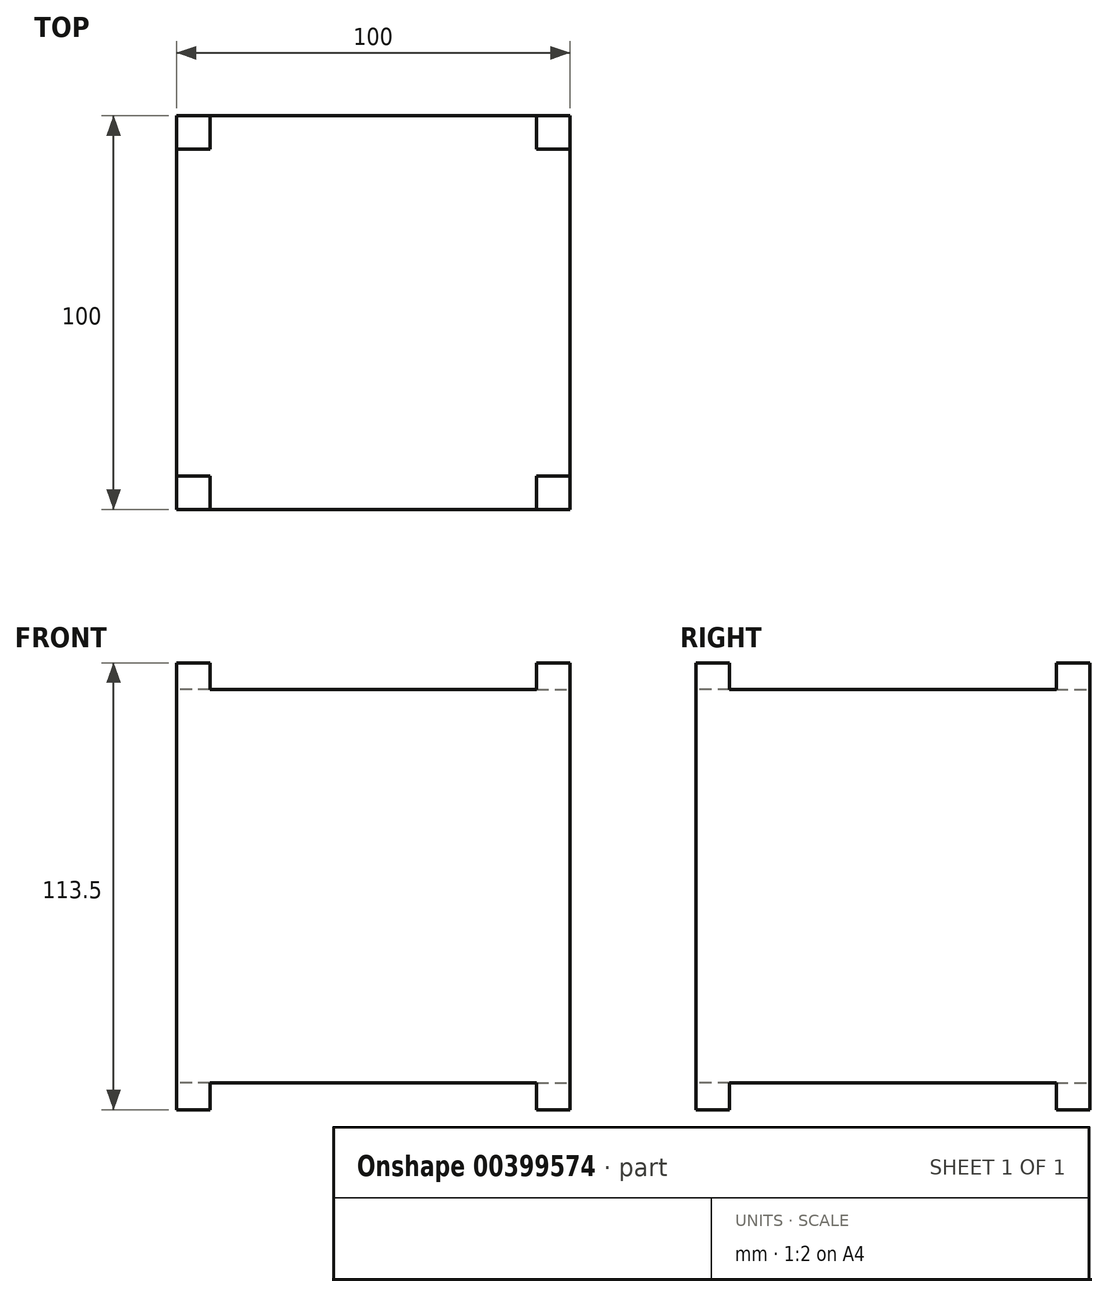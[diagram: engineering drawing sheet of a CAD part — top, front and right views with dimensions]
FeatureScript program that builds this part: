
annotation { "Feature Type Name" : "Feature", "Feature Type Description" : "" }
export const myFeature = defineFeature(function(context is Context, id is Id, definition is map)
    precondition{}
    {
        {
            var Q0;
            Q0=qCreatedBy(makeId("Top.planeOp"),FACE);
            var sketch = newSketch(context, id + "F0", { "sketchPlane" : qUnion([Q0])});
            skLineSegment(sketch, "E0.bottom", {"start": v(-50, 50) * mm, "end": v(50, 50) * mm});
            skLineSegment(sketch, "E0.top", {"start": v(-50, -50) * mm, "end": v(50, -50) * mm});
            skLineSegment(sketch, "E0.left", {"start": v(-50, 50) * mm, "end": v(-50, -50) * mm});
            skLineSegment(sketch, "E0.right", {"start": v(50, 50) * mm, "end": v(50, -50) * mm});
            skSolve(sketch);
        }
        {
            var Q0;
            Q0 = qSketchRegion(id + "F0", true);
            extrude(context, id + "F1", {"entities" : qUnion([Q0]), "endBound" : BoundingType.SYMMETRIC, "depth" : 100 * mm, "offsetDistance" : 25 * mm});
        }
        {
            var Q0;
            Q0=qCreatedBy(makeId("Top.planeOp"),FACE);
            var sketch = newSketch(context, id + "F2", { "sketchPlane" : qUnion([Q0])});
            skLineSegment(sketch, "E1.bottom", {"start": v(-50, 50) * mm, "end": v(-41.5, 50) * mm});
            skLineSegment(sketch, "E1.top", {"start": v(-50, 41.5) * mm, "end": v(-41.5, 41.5) * mm});
            skLineSegment(sketch, "E1.left", {"start": v(-50, 50) * mm, "end": v(-50, 41.5) * mm});
            skLineSegment(sketch, "E1.right", {"start": v(-41.5, 50) * mm, "end": v(-41.5, 41.5) * mm});
            skLineSegment(sketch, "E2.MirrorCS", {"start": v(50, 50) * mm, "end": v(50, 41.5) * mm});
            skLineSegment(sketch, "E3.MirrorCS", {"start": v(41.5, 50) * mm, "end": v(41.5, 41.5) * mm});
            skLineSegment(sketch, "E4.MirrorCS", {"start": v(50, 50) * mm, "end": v(41.5, 50) * mm});
            skLineSegment(sketch, "E5.MirrorCS", {"start": v(50, 41.5) * mm, "end": v(41.5, 41.5) * mm});
            skLineSegment(sketch, "E6.MirrorCS", {"start": v(50, -41.5) * mm, "end": v(41.5, -41.5) * mm});
            skLineSegment(sketch, "E7.MirrorCS", {"start": v(50, -50) * mm, "end": v(50, -41.5) * mm});
            skLineSegment(sketch, "E8.MirrorCS", {"start": v(50, -50) * mm, "end": v(41.5, -50) * mm});
            skLineSegment(sketch, "E9.MirrorCS", {"start": v(41.5, -50) * mm, "end": v(41.5, -41.5) * mm});
            skLineSegment(sketch, "E10.MirrorCS", {"start": v(-50, -50) * mm, "end": v(-50, -41.5) * mm});
            skLineSegment(sketch, "E11.MirrorCS", {"start": v(-41.5, -50) * mm, "end": v(-41.5, -41.5) * mm});
            skLineSegment(sketch, "E12.MirrorCS", {"start": v(-50, -41.5) * mm, "end": v(-41.5, -41.5) * mm});
            skLineSegment(sketch, "E13.MirrorCS", {"start": v(-50, -50) * mm, "end": v(-41.5, -50) * mm});
            skSolve(sketch);
        }
        {
            var Q0;
            Q0 = qSketchRegion(id + "F2", true);
            extrude(context, id + "F3", {"entities" : qUnion([Q0]), "operationType" : NewBodyOperationType.ADD, "endBound" : BoundingType.SYMMETRIC, "depth" : 113.5 * mm, "offsetDistance" : 25 * mm});
        }
    });
